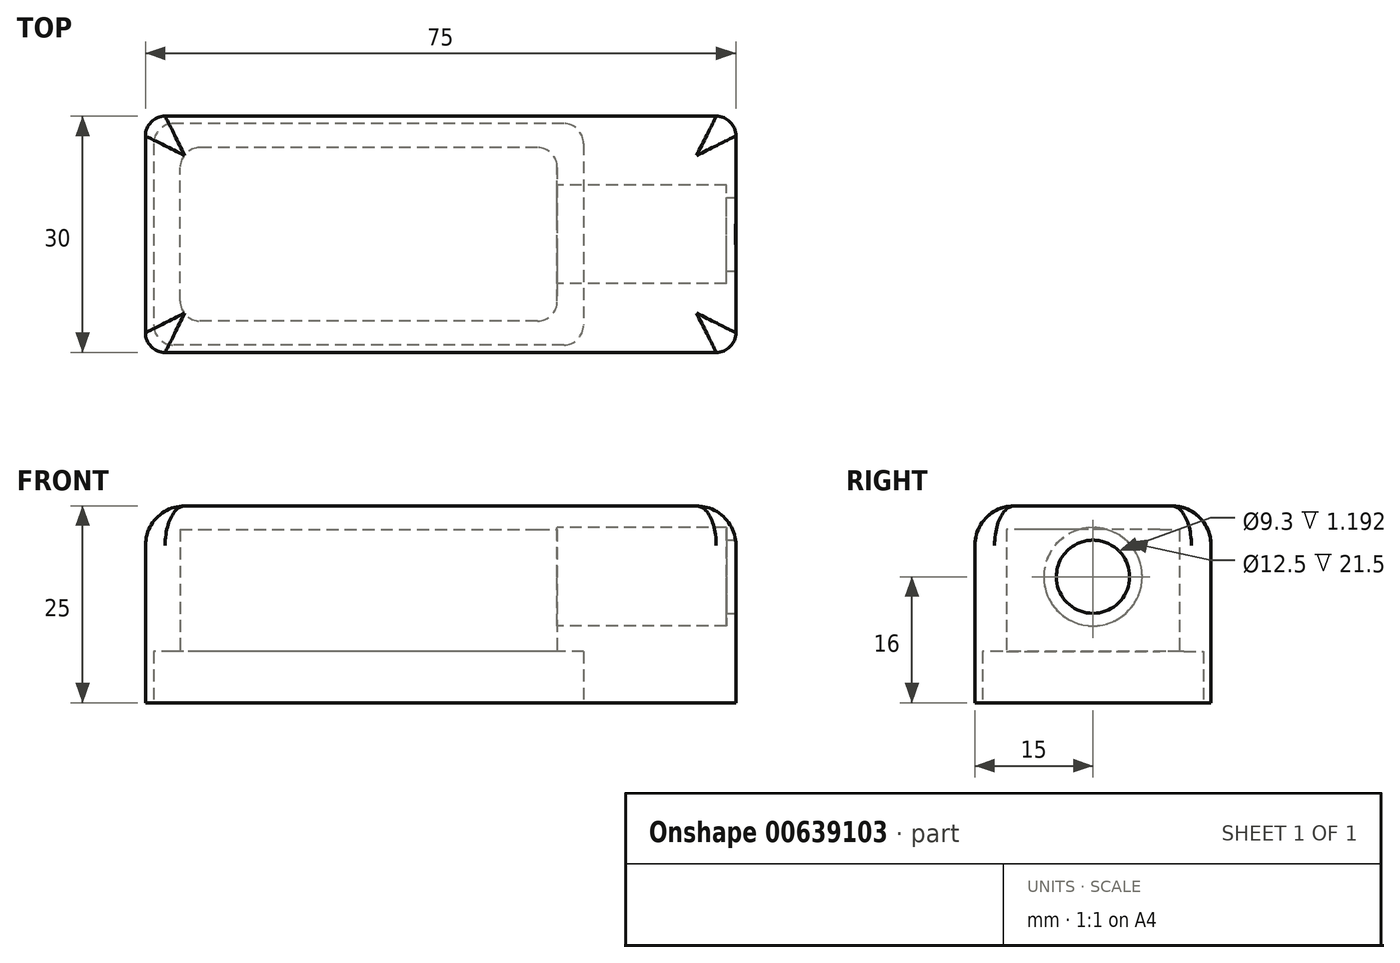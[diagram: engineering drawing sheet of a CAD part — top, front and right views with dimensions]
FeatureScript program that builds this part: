
annotation { "Feature Type Name" : "Feature", "Feature Type Description" : "" }
export const myFeature = defineFeature(function(context is Context, id is Id, definition is map)
    precondition{}
    {
        {
            var Q0;
            Q0=qCreatedBy(makeId("Top.planeOp"),FACE);
            var sketch = newSketch(context, id + "F0", { "sketchPlane" : qUnion([Q0])});
            skLineSegment(sketch, "E0.bottom", {"start": v(-35, 15) * mm, "end": v(35, 15) * mm});
            skLineSegment(sketch, "E0.top", {"start": v(-35, -15) * mm, "end": v(35, -15) * mm});
            skLineSegment(sketch, "E0.left", {"start": v(-37.5, 12.5) * mm, "end": v(-37.5, -12.5) * mm});
            skLineSegment(sketch, "E0.right", {"start": v(37.5, 12.5) * mm, "end": v(37.5, -12.5) * mm});
            skPoint(sketch, "E0.middle", {"position": v(0, 0) * mm});
            skPoint(sketch, "E1.visualSharp", {"position": v(-37.5, 15) * mm});
            skArc(sketch, "E1.filletArc", {"start": v(-35, 15) * mm, "mid": v(-36.77, 14.27) * mm, "end": v(-37.5, 12.5) * mm});
            skPoint(sketch, "E2.visualSharp", {"position": v(-37.5, -15) * mm});
            skArc(sketch, "E2.filletArc", {"start": v(-37.5, -12.5) * mm, "mid": v(-36.77, -14.27) * mm, "end": v(-35, -15) * mm});
            skPoint(sketch, "E3.visualSharp", {"position": v(37.5, -15) * mm});
            skArc(sketch, "E3.filletArc", {"start": v(35, -15) * mm, "mid": v(36.77, -14.27) * mm, "end": v(37.5, -12.5) * mm});
            skPoint(sketch, "E4.visualSharp", {"position": v(37.5, 15) * mm});
            skArc(sketch, "E4.filletArc", {"start": v(37.5, 12.5) * mm, "mid": v(36.77, 14.27) * mm, "end": v(35, 15) * mm});
            skSolve(sketch);
        }
        {
            var Q0;
            Q0 = qSketchRegion(id + "F0", true);
            extrude(context, id + "F1", {"entities" : qUnion([Q0]), "depth" : 25 * mm, "offsetDistance" : 25 * mm});
        }
        {
            var Q0;
            Q0=makeQuery(id+"F1.opExtrude","CAP_FACE",FACE,{"disambiguationData":[OSD([sQuery(id+"F0.wireOp",EDGE,"E0.bottom"),sQuery(id+"F0.wireOp",EDGE,"E0.top"),sQuery(id+"F0.wireOp",EDGE,"E0.left"),sQuery(id+"F0.wireOp",EDGE,"E0.right"),sQuery(id+"F0.wireOp",EDGE,"E1.filletArc"),sQuery(id+"F0.wireOp",EDGE,"E2.filletArc"),sQuery(id+"F0.wireOp",EDGE,"E3.filletArc"),sQuery(id+"F0.wireOp",EDGE,"E4.filletArc")])],"isStart":true});
            var sketch = newSketch(context, id + "F2", { "sketchPlane" : qUnion([Q0])});
            skLineSegment(sketch, "E5.bottom", {"start": v(-30.6, -11) * mm, "end": v(12.3, -11) * mm});
            skLineSegment(sketch, "E5.top", {"start": v(-30.6, 11) * mm, "end": v(12.3, 11) * mm});
            skLineSegment(sketch, "E5.left", {"start": v(-33.1, -8.5) * mm, "end": v(-33.1, 8.5) * mm});
            skLineSegment(sketch, "E5.right", {"start": v(14.8, -8.5) * mm, "end": v(14.8, 8.5) * mm});
            skPoint(sketch, "E5.middle", {"position": v(-9.14, 0) * mm});
            skPoint(sketch, "E6.visualSharp", {"position": v(-33.1, 11) * mm});
            skArc(sketch, "E6.filletArc", {"start": v(-30.6, 11) * mm, "mid": v(-32.36, 10.27) * mm, "end": v(-33.1, 8.5) * mm});
            skPoint(sketch, "E7.visualSharp", {"position": v(-33.1, -11) * mm});
            skArc(sketch, "E7.filletArc", {"start": v(-33.1, -8.5) * mm, "mid": v(-32.36, -10.27) * mm, "end": v(-30.6, -11) * mm});
            skPoint(sketch, "E8.visualSharp", {"position": v(14.8, -11) * mm});
            skArc(sketch, "E8.filletArc", {"start": v(12.3, -11) * mm, "mid": v(14.08, -10.27) * mm, "end": v(14.8, -8.5) * mm});
            skPoint(sketch, "E9.visualSharp", {"position": v(14.8, 11) * mm});
            skArc(sketch, "E9.filletArc", {"start": v(14.8, 8.5) * mm, "mid": v(14.08, 10.27) * mm, "end": v(12.3, 11) * mm});
            skSolve(sketch);
        }
        {
            var Q0;
            Q0 = qSketchRegion(id + "F2", true);
            extrude(context, id + "F3", {"entities" : qUnion([Q0]), "operationType" : NewBodyOperationType.REMOVE, "oppositeDirection" : true, "depth" : 22 * mm, "offsetDistance" : 25 * mm});
        }
        {
            var Q0;
            Q0=makeQuery(id+"F1.opExtrude","CAP_FACE",FACE,{"disambiguationData":[OSD([sQuery(id+"F0.wireOp",EDGE,"E0.bottom"),sQuery(id+"F0.wireOp",EDGE,"E0.top"),sQuery(id+"F0.wireOp",EDGE,"E0.left"),sQuery(id+"F0.wireOp",EDGE,"E0.right"),sQuery(id+"F0.wireOp",EDGE,"E1.filletArc"),sQuery(id+"F0.wireOp",EDGE,"E2.filletArc"),sQuery(id+"F0.wireOp",EDGE,"E3.filletArc"),sQuery(id+"F0.wireOp",EDGE,"E4.filletArc")])],"isStart":true});
            var sketch = newSketch(context, id + "F4", { "sketchPlane" : qUnion([Q0])});
            skLineSegment(sketch, "E10.bottom", {"start": v(15.66, -14.05) * mm, "end": v(-33.94, -14.05) * mm});
            skLineSegment(sketch, "E10.top", {"start": v(15.66, 14.05) * mm, "end": v(-33.94, 14.05) * mm});
            skLineSegment(sketch, "E10.left", {"start": v(18.16, -11.55) * mm, "end": v(18.16, 11.55) * mm});
            skLineSegment(sketch, "E10.right", {"start": v(-36.44, -11.55) * mm, "end": v(-36.44, 11.55) * mm});
            skPoint(sketch, "E10.middle", {"position": v(-9.14, 0) * mm});
            skPoint(sketch, "E10.middle.positionSnap0", {"position": v(-9.14, -11) * mm});
            skPoint(sketch, "E10.centerSnap0", {"position": v(-9.14, -11) * mm});
            skPoint(sketch, "E11.visualSharp", {"position": v(-36.44, 14.05) * mm});
            skArc(sketch, "E11.filletArc", {"start": v(-33.94, 14.05) * mm, "mid": v(-35.7, 13.32) * mm, "end": v(-36.44, 11.55) * mm});
            skPoint(sketch, "E12.visualSharp", {"position": v(18.16, 14.05) * mm});
            skArc(sketch, "E12.filletArc", {"start": v(18.16, 11.55) * mm, "mid": v(17.43, 13.32) * mm, "end": v(15.66, 14.05) * mm});
            skPoint(sketch, "E13.visualSharp", {"position": v(18.16, -14.05) * mm});
            skArc(sketch, "E13.filletArc", {"start": v(15.66, -14.05) * mm, "mid": v(17.43, -13.32) * mm, "end": v(18.16, -11.55) * mm});
            skPoint(sketch, "E14.visualSharp", {"position": v(-36.44, -14.05) * mm});
            skArc(sketch, "E14.filletArc", {"start": v(-36.44, -11.55) * mm, "mid": v(-35.7, -13.32) * mm, "end": v(-33.94, -14.05) * mm});
            skSolve(sketch);
        }
        {
            var Q0;
            Q0 = qSketchRegion(id + "F4", true);
            extrude(context, id + "F5", {"entities" : qUnion([Q0]), "operationType" : NewBodyOperationType.REMOVE, "oppositeDirection" : true, "depth" : 6.5 * mm, "offsetDistance" : 25 * mm});
        }
        {
            var Q0;
            Q0=makeQuery(id+"F1.opExtrude","SWEPT_FACE",FACE,{"disambiguationData":[OSD([sQuery(id+"F0.wireOp",EDGE,"E0.right")])]});
            var sketch = newSketch(context, id + "F6", { "sketchPlane" : qUnion([Q0])});
            skPoint(sketch, "E15.centerSnap0", {"position": v(-12.5, 12.5) * mm});
            skCircle(sketch, "E16", {"center": v(0, 16) * mm, "radius": 4.65 * mm});
            skSolve(sketch);
        }
        {
            var Q0;
            Q0 = qSketchRegion(id + "F6", true);
            extrude(context, id + "F7", {"entities" : qUnion([Q0]), "operationType" : NewBodyOperationType.REMOVE, "oppositeDirection" : true, "depth" : 25 * mm, "offsetDistance" : 25 * mm});
        }
        {
            var Q0;
            Q0=makeQuery(id+"F1.opExtrude","CAP_EDGE",EDGE,{"disambiguationData":[OSD([sQuery(id+"F0.wireOp",EDGE,"E0.top")])],"isStart":false});
            fillet(context, id + "F8", {"entities" : qUnion([Q0]), "radius" : 5 * mm, "tangentPropagation" : true, "allowEdgeOverflow" : false});
        }
        {
            var Q0;
            Q0=makeQuery(id+"F3.boolean.opBoolean","COPY",FACE,{"derivedFrom":makeQuery(id+"F3.opExtrude","SWEPT_FACE",FACE,{"disambiguationData":[OSD([sQuery(id+"F2.wireOp",EDGE,"E5.right")])]})});
            var sketch = newSketch(context, id + "F9", { "sketchPlane" : qUnion([Q0])});
            skCircle(sketch, "E17", {"center": v(0, 16) * mm, "radius": 6.25 * mm});
            skSolve(sketch);
        }
        {
            var Q0;
            Q0 = qSketchRegion(id + "F9", true);
            extrude(context, id + "F10", {"entities" : qUnion([Q0]), "operationType" : NewBodyOperationType.REMOVE, "oppositeDirection" : true, "depth" : 21.5 * mm, "offsetDistance" : 25 * mm});
        }
    });
